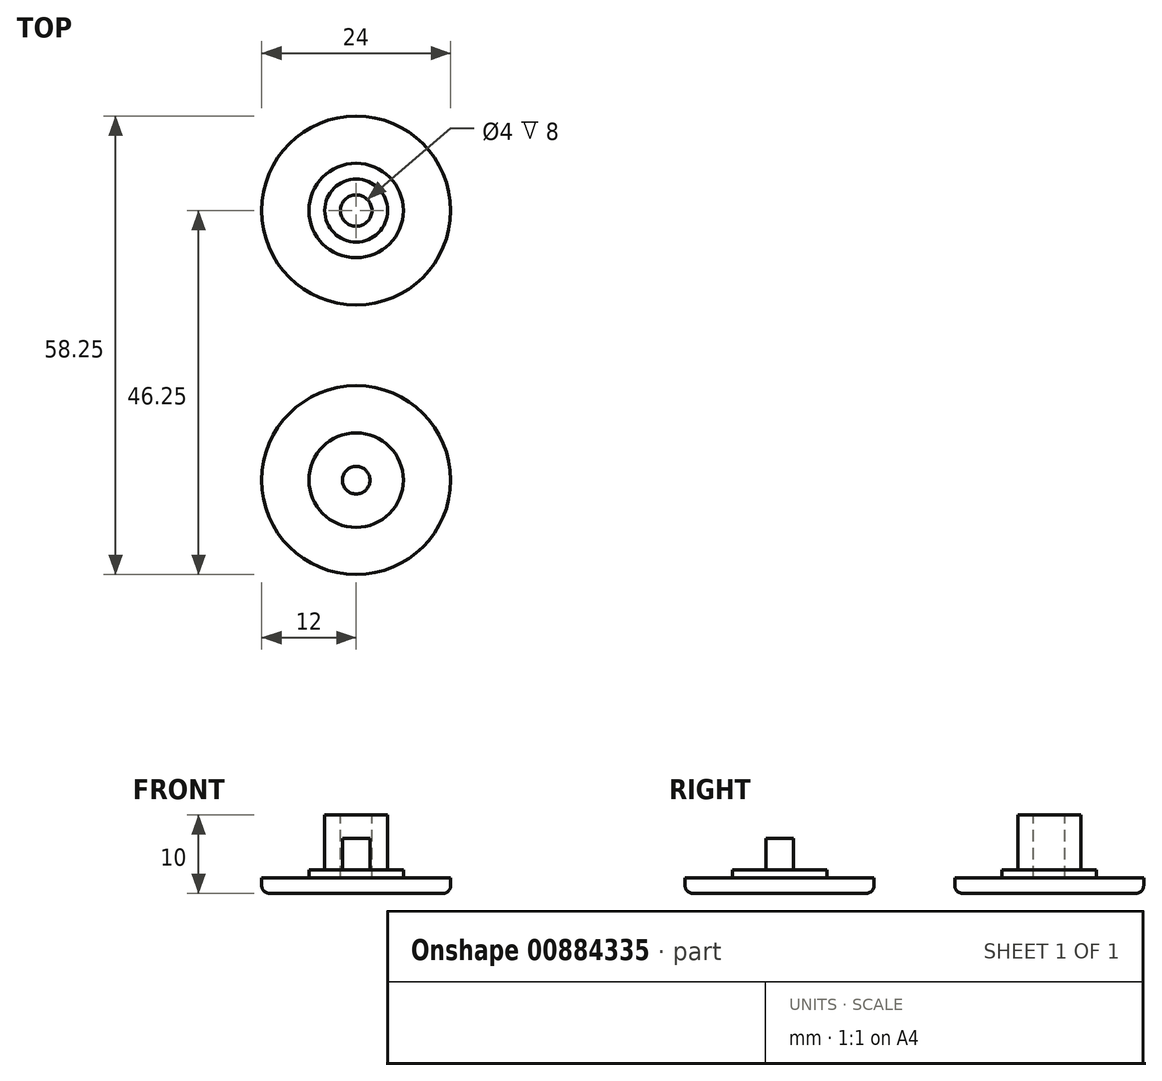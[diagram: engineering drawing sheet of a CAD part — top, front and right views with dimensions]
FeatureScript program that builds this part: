
annotation { "Feature Type Name" : "Feature", "Feature Type Description" : "" }
export const myFeature = defineFeature(function(context is Context, id is Id, definition is map)
    precondition{}
    {
        {
            var Q0;
            Q0=qCreatedBy(makeId("Top.planeOp"),FACE);
            var sketch = newSketch(context, id + "F0", { "sketchPlane" : qUnion([Q0])});
            skCircle(sketch, "E0", {"center": v(0, 0) * mm, "radius": 12 * mm});
            skCircle(sketch, "E1", {"center": v(0, 0) * mm, "radius": 6 * mm});
            skCircle(sketch, "E2", {"center": v(0, 0) * mm, "radius": 4 * mm});
            skCircle(sketch, "E3", {"center": v(0, -34.25) * mm, "radius": 12 * mm});
            skCircle(sketch, "E4", {"center": v(0, -34.25) * mm, "radius": 6 * mm});
            skCircle(sketch, "E5", {"center": v(0, -34.25) * mm, "radius": 1.75 * mm});
            skCircle(sketch, "E6", {"center": v(0, 0) * mm, "radius": 2 * mm});
            skSolve(sketch);
        }
        {
            var Q0;
            Q0=makeQuery(id+"F0.imprint","IMPRINT",FACE,{"disambiguationData":[TD([[makeQuery(id+"F0.imprint","IMPRINT",EDGE,{"derivedFrom":sQuery(id+"F0.wireOp",EDGE,"E0")}),1.0]])]});
            var Q1;
            Q1=makeQuery(id+"F0.imprint","IMPRINT",FACE,{"disambiguationData":[TD([[makeQuery(id+"F0.imprint","IMPRINT",EDGE,{"derivedFrom":sQuery(id+"F0.wireOp",EDGE,"E1")}),1.0]])]});
            var Q2;
            Q2=makeQuery(id+"F0.imprint","IMPRINT",FACE,{"disambiguationData":[TD([[makeQuery(id+"F0.imprint","IMPRINT",EDGE,{"derivedFrom":sQuery(id+"F0.wireOp",EDGE,"E2")}),1.0]])]});
            extrude(context, id + "F1", {"entities" : qUnion([Q0, Q1, Q2]), "oppositeDirection" : true, "depth" : 2 * mm, "offsetDistance" : 25 * mm});
        }
        {
            var Q0;
            Q0=makeQuery(id+"F0.imprint","IMPRINT",FACE,{"disambiguationData":[TD([[makeQuery(id+"F0.imprint","IMPRINT",EDGE,{"derivedFrom":sQuery(id+"F0.wireOp",EDGE,"E1")}),1.0]])]});
            var Q1;
            Q1=makeQuery(id+"F0.imprint","IMPRINT",FACE,{"disambiguationData":[TD([[makeQuery(id+"F0.imprint","IMPRINT",EDGE,{"derivedFrom":sQuery(id+"F0.wireOp",EDGE,"E2")}),1.0]])]});
            extrude(context, id + "F2", {"entities" : qUnion([Q0, Q1]), "operationType" : NewBodyOperationType.ADD, "depth" : 1 * mm, "offsetDistance" : 25 * mm});
        }
        {
            var Q0;
            Q0=makeQuery(id+"F0.imprint","IMPRINT",FACE,{"disambiguationData":[TD([[makeQuery(id+"F0.imprint","IMPRINT",EDGE,{"derivedFrom":sQuery(id+"F0.wireOp",EDGE,"E2")}),1.0]])]});
            extrude(context, id + "F3", {"entities" : qUnion([Q0]), "operationType" : NewBodyOperationType.ADD, "depth" : 8 * mm, "offsetDistance" : 25 * mm});
        }
        {
            var Q0;
            Q0=makeQuery(id+"F1.opExtrude","CAP_EDGE",EDGE,{"disambiguationData":[OSD([sQuery(id+"F0.wireOp",EDGE,"E0")])],"isStart":false});
            fillet(context, id + "F4", {"entities" : qUnion([Q0]), "radius" : 1 * mm, "tangentPropagation" : true, "allowEdgeOverflow" : false});
        }
        {
            var Q0;
            Q0=makeQuery(id+"F0.imprint","IMPRINT",FACE,{"disambiguationData":[TD([[makeQuery(id+"F0.imprint","IMPRINT",EDGE,{"derivedFrom":sQuery(id+"F0.wireOp",EDGE,"E3")}),1.0]])]});
            extrude(context, id + "F5", {"entities" : qUnion([Q0]), "oppositeDirection" : true, "depth" : 2 * mm, "offsetDistance" : 25 * mm});
        }
        {
            var Q0;
            Q0=makeQuery(id+"F0.imprint","IMPRINT",FACE,{"disambiguationData":[TD([[makeQuery(id+"F0.imprint","IMPRINT",EDGE,{"derivedFrom":sQuery(id+"F0.wireOp",EDGE,"E4")}),1.0]])]});
            extrude(context, id + "F6", {"entities" : qUnion([Q0]), "operationType" : NewBodyOperationType.ADD, "depth" : 1 * mm, "offsetDistance" : 25 * mm, "hasSecondDirection" : true, "secondDirectionOppositeDirection" : true, "secondDirectionDepth" : 2 * mm});
        }
        {
            var Q0;
            Q0=makeQuery(id+"F0.imprint","IMPRINT",FACE,{"disambiguationData":[TD([[makeQuery(id+"F0.imprint","IMPRINT",EDGE,{"derivedFrom":sQuery(id+"F0.wireOp",EDGE,"E5")}),1.0]])]});
            extrude(context, id + "F7", {"entities" : qUnion([Q0]), "operationType" : NewBodyOperationType.ADD, "depth" : 5 * mm, "offsetDistance" : 25 * mm, "hasSecondDirection" : true, "secondDirectionOppositeDirection" : true, "secondDirectionDepth" : 2 * mm});
        }
        {
            var Q0;
            Q0=makeQuery(id+"F0.imprint","IMPRINT",FACE,{"disambiguationData":[TD([[makeQuery(id+"F0.imprint","IMPRINT",EDGE,{"derivedFrom":sQuery(id+"F0.wireOp",EDGE,"E6")}),1.0]])]});
            extrude(context, id + "F8", {"entities" : qUnion([Q0]), "operationType" : NewBodyOperationType.ADD, "oppositeDirection" : true, "depth" : 2 * mm, "offsetDistance" : 25 * mm});
        }
        {
            var Q0;
            Q0=makeQuery(id+"F5.opExtrude","CAP_EDGE",EDGE,{"disambiguationData":[OSD([sQuery(id+"F0.wireOp",EDGE,"E3")])],"isStart":false});
            fillet(context, id + "F9", {"entities" : qUnion([Q0]), "radius" : 1 * mm, "tangentPropagation" : true, "allowEdgeOverflow" : false});
        }
    });
